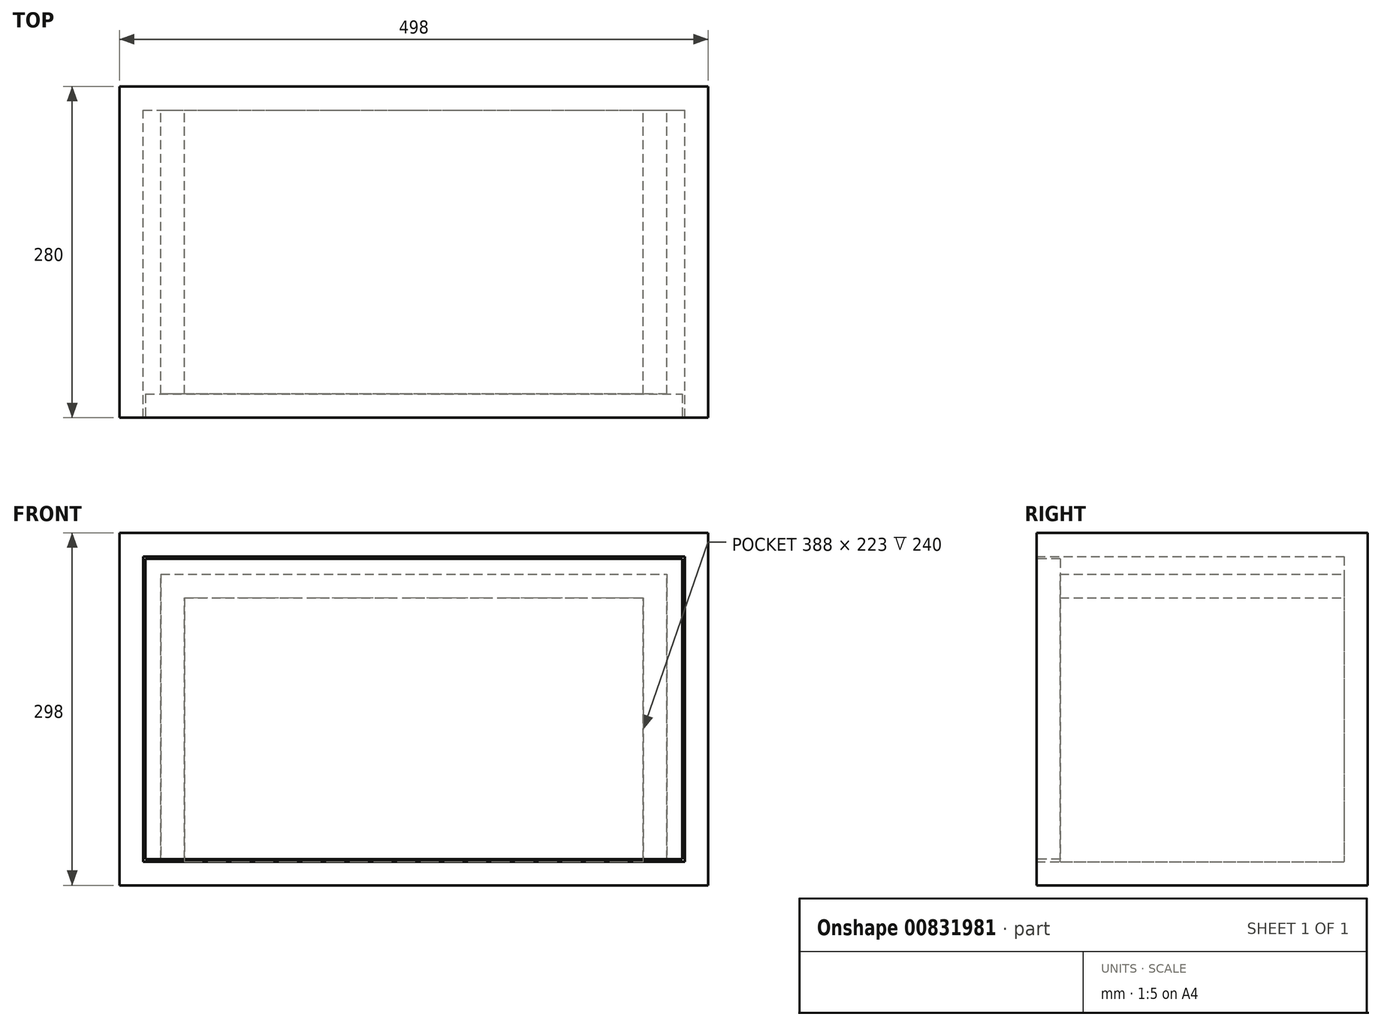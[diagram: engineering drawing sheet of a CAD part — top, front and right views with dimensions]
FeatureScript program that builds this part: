
annotation { "Feature Type Name" : "Feature", "Feature Type Description" : "" }
export const myFeature = defineFeature(function(context is Context, id is Id, definition is map)
    precondition{}
    {
        {
            var Q0;
            Q0=qCreatedBy(makeId("Top.planeOp"),FACE);
            var sketch = newSketch(context, id + "F0", { "sketchPlane" : qUnion([Q0])});
            skLineSegment(sketch, "E0.bottom", {"start": v(0, 0) * mm, "end": v(498, 0) * mm});
            skLineSegment(sketch, "E0.top", {"start": v(0, 280) * mm, "end": v(498, 280) * mm});
            skLineSegment(sketch, "E0.left", {"start": v(0, 0) * mm, "end": v(0, 280) * mm});
            skLineSegment(sketch, "E0.right", {"start": v(498, 0) * mm, "end": v(498, 280) * mm});
            skSolve(sketch);
        }
        {
            var Q0;
            Q0=makeQuery(id+"F0.imprint","IMPRINT",FACE,{"disambiguationData":[TD([[makeQuery(id+"F0.imprint","IMPRINT",EDGE,{"derivedFrom":sQuery(id+"F0.wireOp",EDGE,"E0.bottom")}),1.0]])]});
            extrude(context, id + "F1", {"entities" : qUnion([Q0]), "depth" : 298 * mm, "offsetDistance" : 25 * mm});
        }
        {
            var Q0;
            Q0=makeQuery(id+"F1.opExtrude","SWEPT_FACE",FACE,{"disambiguationData":[OSD([sQuery(id+"F0.wireOp",EDGE,"E0.bottom")])]});
            shell(context, id + "F2", {"entities" : qUnion([Q0]), "thickness" : 20 * mm});
        }
        {
            var Q0;
            Q0=makeQuery(id+"F2.opShell","OFFSET_FACE",FACE,{"disambiguationData":[OSD([sQuery(id+"F0.wireOp",EDGE,"E0.top")])]});
            var sketch = newSketch(context, id + "F3", { "sketchPlane" : qUnion([Q0])});
            skLineSegment(sketch, "E1.0", {"start": v(35, 263) * mm, "end": v(463, 263) * mm});
            skLineSegment(sketch, "E1.1", {"start": v(35, 263) * mm, "end": v(35, 20) * mm});
            skLineSegment(sketch, "E1.3", {"start": v(463, 263) * mm, "end": v(463, 20) * mm});
            skLineSegment(sketch, "E2.0", {"start": v(55, 243) * mm, "end": v(55, 20) * mm});
            skLineSegment(sketch, "E2.1", {"start": v(55, 243) * mm, "end": v(443, 243) * mm});
            skLineSegment(sketch, "E2.2", {"start": v(443, 243) * mm, "end": v(443, 20) * mm});
            skSolve(sketch);
        }
        {
            var Q0;
            Q0=makeQuery(id+"F3.imprint","IMPRINT",FACE,{"disambiguationData":[TD([[makeQuery(id+"F3.imprint","IMPRINT",EDGE,{"derivedFrom":sQuery(id+"F3.wireOp",EDGE,"E1.0")}),-1.0]])]});
            var Q1;
            Q1=makeQuery(id+"F1.opExtrude","SWEPT_FACE",FACE,{"disambiguationData":[OSD([sQuery(id+"F0.wireOp",EDGE,"E0.bottom")])]});
            extrude(context, id + "F4", {"entities" : qUnion([Q0]), "operationType" : NewBodyOperationType.ADD, "endBound" : BoundingType.UP_TO_SURFACE, "depth" : 25 * mm, "endBoundEntityFace" : qUnion([Q1]), "hasOffset" : true, "offsetDistance" : 20 * mm});
        }
        {
            var Q0;
            Q0=makeQuery(id+"F1.opExtrude","SWEPT_FACE",FACE,{"disambiguationData":[OSD([sQuery(id+"F0.wireOp",EDGE,"E0.bottom")])]});
            var sketch = newSketch(context, id + "F5", { "sketchPlane" : qUnion([Q0])});
            skLineSegment(sketch, "E3.0", {"start": v(22, 276) * mm, "end": v(476, 276) * mm});
            skLineSegment(sketch, "E3.1", {"start": v(22, 276) * mm, "end": v(22, 22) * mm});
            skLineSegment(sketch, "E3.2", {"start": v(22, 22) * mm, "end": v(476, 22) * mm});
            skLineSegment(sketch, "E3.3", {"start": v(476, 276) * mm, "end": v(476, 22) * mm});
            skSolve(sketch);
        }
        {
            var Q0;
            Q0=makeQuery(id+"F5.imprint","IMPRINT",FACE,{"disambiguationData":[TD([[makeQuery(id+"F5.imprint","IMPRINT",EDGE,{"derivedFrom":sQuery(id+"F5.wireOp",EDGE,"E3.0")}),-1.0]])]});
            extrude(context, id + "F6", {"entities" : qUnion([Q0]), "oppositeDirection" : true, "depth" : 20 * mm, "offsetDistance" : 25 * mm});
        }
    });
